FCSTD DOCUMENT  (FreeCAD 1.0R39285 (Git))
Label: L-Boxx_Templates
License: All rights reserved
LicenseURL: https://en.wikipedia.org/wiki/All_rights_reserved
objects: Sketcher::SketchObject×1, PartDesign::Body×1, Spreadsheet::Sheet×1
note: 3 computed .brp shape members not serialized (recipe doc carries the construction recipe); baked Part::Feature solids carry a one-line shape summary decoded from their .brp

FEATURE [Sketcher::SketchObject] Sketch  label="L_Boxx_238_Bottom_Inlay_Sketch"
  ArcFitTolerance = 1e-06
  AttachmentSupport = -> [XY_Plane]
  FullyConstrained = true
  MakeInternals = false
  MapMode = 5
  expr: Constraints[23] = 304 mm - 2 * <<config>>.clearance
  expr: Constraints[24] = 393 mm - 2 * <<config>>.clearance
  expr: Constraints[35] = 378 mm - 2 * <<config>>.clearance
  expr: Constraints[36] = 84 mm - <<config>>.clearance
  sketch-geometry (28):
    g0: LineSegment StartX=-191 StartY=151.5 StartZ=0 EndX=191 EndY=151.5 EndZ=0
    g1: LineSegment StartX=196 StartY=146.5 StartZ=0 EndX=196 EndY=68 EndZ=0
    g2: LineSegment StartX=196 StartY=68 StartZ=0 EndX=188.5 EndY=68 EndZ=0
    g3: LineSegment StartX=188.5 StartY=68 StartZ=0 EndX=188.5 EndY=-68 EndZ=0
    g4: LineSegment StartX=188.5 StartY=-68 StartZ=0 EndX=196 EndY=-68 EndZ=0
    g5: LineSegment StartX=196 StartY=-68 StartZ=0 EndX=196 EndY=-146.5 EndZ=0
    g6: LineSegment StartX=191 StartY=-151.5 StartZ=0 EndX=-191 EndY=-151.5 EndZ=0
    g7: LineSegment StartX=-196 StartY=-146.5 StartZ=0 EndX=-196 EndY=-68 EndZ=0
    g8: LineSegment StartX=-196 StartY=-68 StartZ=0 EndX=-188.5 EndY=-68 EndZ=0
    g9: LineSegment StartX=-188.5 StartY=-68 StartZ=0 EndX=-188.5 EndY=68 EndZ=0
    g10: LineSegment StartX=-188.5 StartY=68 StartZ=0 EndX=-196 EndY=68 EndZ=0
    g11: LineSegment StartX=-196 StartY=68 StartZ=0 EndX=-196 EndY=146.5 EndZ=0
    g12: LineSegment [constr] StartX=-196 StartY=151.5 StartZ=0 EndX=0 EndY=0 EndZ=0
    g13: LineSegment [constr] StartX=0 StartY=0 StartZ=0 EndX=196 EndY=-151.5 EndZ=0
    g14: LineSegment [constr] StartX=196 StartY=151.5 StartZ=0 EndX=0 EndY=0 EndZ=0
    g15: LineSegment [constr] StartX=0 StartY=0 StartZ=0 EndX=-196 EndY=-151.5 EndZ=0
    g16: ArcOfCircle CenterX=-191 CenterY=146.5 CenterZ=0 NormalX=0 NormalY=0 NormalZ=1 AngleXU=0 Radius=5 StartAngle=1.5708 EndAngle=3.14159
    g17: GeomPoint [constr] X=-196 Y=151.5 Z=0
    g18: ArcOfCircle CenterX=191 CenterY=146.5 CenterZ=0 NormalX=0 NormalY=0 NormalZ=1 AngleXU=0 Radius=5 StartAngle=4e-16 EndAngle=1.5708
    g19: GeomPoint [constr] X=196 Y=151.5 Z=0
    g20: ArcOfCircle CenterX=191 CenterY=-146.5 CenterZ=0 NormalX=0 NormalY=0 NormalZ=1 AngleXU=0 Radius=5 StartAngle=4.71239 EndAngle=6.28319
    g21: GeomPoint [constr] X=196 Y=-151.5 Z=0
    g22: ArcOfCircle CenterX=-191 CenterY=-146.5 CenterZ=0 NormalX=0 NormalY=0 NormalZ=1 AngleXU=0 Radius=5 StartAngle=3.14159 EndAngle=4.71239
    g23: GeomPoint [constr] X=-196 Y=-151.5 Z=0
    g24: LineSegment [constr] StartX=0 StartY=0 StartZ=0 EndX=-100 EndY=0 EndZ=0
    g25: LineSegment [constr] StartX=0 StartY=0 StartZ=0 EndX=100 EndY=0 EndZ=0
    g26: Circle CenterX=-100 CenterY=0 CenterZ=0 NormalX=0 NormalY=0 NormalZ=1 AngleXU=0 Radius=2
    g27: Circle CenterX=100 CenterY=0 CenterZ=0 NormalX=0 NormalY=0 NormalZ=1 AngleXU=0 Radius=2
  constraints (70):
    c: Horizontal(g0)
    c: Vertical(g1)
    c: Coincident(g1,g2)
    c: Coincident(g2,g3)
    c: Vertical(g3)
    c: Coincident(g3,g4)
    c: Coincident(g4,g5)
    c: Vertical(g5)
    c: Horizontal(g6)
    c: Vertical(g7)
    c: Coincident(g7,g8)
    c: Horizontal(g8)
    c: Coincident(g8,g9)
    c: Vertical(g9)
    c: Coincident(g9,g10)
    c: Horizontal(g10)
    c: Coincident(g10,g11)
    c: Vertical(g11)
    c: Horizontal(g4)
    c: Horizontal(g2)
    c: Equal(g10,g2)
    c: Equal(g10,g8)
    c: Equal(g2,g4)
    c: DistanceY(g21,g19) = 303
    c: DistanceX(g23,g21) = 392
    c: Coincident(g17,g12)
    c: Coincident(g12,g-1)
    c: Coincident(g12,g13)
    c: Coincident(g13,g21)
    c: Coincident(g19,g14)
    c: Coincident(g14,g12)
    c: Coincident(g14,g15)
    c: Coincident(g15,g23)
    c: Equal(g12,g14)
    c: Equal(g13,g14)
    c: DistanceX(g8,g3) = 377
    c: DistanceY(g11,g17) = 83.5
    c: PointOnObject(g17,g0)
    c: PointOnObject(g17,g11)
    c: Tangent(g0,g16) = 1.5708
    c: Tangent(g11,g16) = 1.5708
    c: PointOnObject(g19,g0)
    c: PointOnObject(g19,g1)
    c: Tangent(g0,g18) = 1.5708
    c: Tangent(g1,g18) = 1.5708
    c: PointOnObject(g21,g5)
    c: PointOnObject(g21,g6)
    c: Tangent(g5,g20) = 1.5708
    c: Tangent(g6,g20) = 1.5708
    c: PointOnObject(g23,g6)
    c: PointOnObject(g23,g7)
    c: Tangent(g6,g22) = 1.5708
    c: Tangent(g7,g22) = 1.5708
    c: Radius(g16) = 5
    c: Equal(g16,g18)
    c: Equal(g16,g20)
    c: Equal(g16,g22)
    c: Equal(g11,g7)
    c: Equal(g1,g11)
    c: Equal(g5,g1)
    c: Coincident(g24,g12)
    c: PointOnObject(g24,g-1)
    c: Coincident(g25,g12)
    c: PointOnObject(g25,g-1)
    c: Equal(g24,g25)
    c: Diameter(g26) = 4
    c: Coincident(g27,g25)
    c: Equal(g27,g26)
    c: Coincident(g26,g24)
    c: DistanceX(g24,g24) = 100
FEATURE [PartDesign::Body] Body
  AllowCompound = false
  Group = -> [Sketch]
  Origin = -> Origin
FEATURE [Spreadsheet::Sheet] Spreadsheet  label="config"
  cells = A1='clearance; B1(clearance)==0.5 mm
